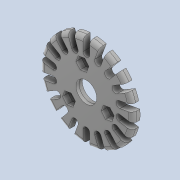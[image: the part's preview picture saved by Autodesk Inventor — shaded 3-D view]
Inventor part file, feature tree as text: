
AUTODESK INVENTOR PART (.ipt)
format: ipt  version: 2020.4 (Build 244396000, 396)  size: 416,256 bytes
history: native  units: mm
features: sketch x6, extrude x4, hole x2, fillet x1
ambient origin geometry x8: Origin, YZ Plane, XZ Plane, XY Plane, X Axis, Y Axis, Z Axis, Center Point
bodies: Solid1 (feature_tree)
feature tree (13):
  extrude  "PartB Base"  Depth=3.5mm TaperAngle=0.0deg
  extrude  "Roller Entrance"  Depth=3.2mm
  hole  "Bearing Fit"  [1 undecoded]
  extrude  "Threads Fit"  Depth=10.0mm TaperAngle=0.0deg
  extrude  "Extrusion4"  Depth=2.0mm
  hole  "Thread Fit"  [1 undecoded]
  fillet  "Ground Round"  Radius=30.0mm
  sketch  "Sketch1"  dims[d0=45.0mm d1=3.5mm d2=0.0mm]
  sketch  "Sketch2"  dims[d3=6.7mm d4=3.2mm]
  sketch  "Sketch3"  dims[d5=0.0mm d6=19.6mm]
  sketch  "Sketch4"  dims[d7=180.0mm d9=360.0deg d11=10.0mm d12=0.0mm]
  sketch  "Sketch5"  dims[d13=11.0mm d14=6.0mm d15=4.0mm d16=2.0mm d17=90.0deg d18=2.0mm d19=0.0mm d20=3.0mm]
  sketch  "Sketch6"  dims[d21=1.91013mm d22=10.833mm d23=30.0mm d25=360.0deg d27=10.0mm d28=0.0mm d29=2.76mm d30=2.76mm d31=2.76mm d32=2.75mm d33=0.0mm d34=10.0mm d35=6.0mm d36=4.0mm d37=2.0mm d38=90.0deg d39=1.5mm d40=0.0mm d41=2.0mm]
note: 2 required parameter values undecoded (feature->parameter linkage not recoverable at this tier; creation-order binding heuristic only, values carry confidence <= 0.55)
